# Revit family: Screen-Beam_Mounted-Teknion-JNSAFB_Fabric_Add-On-R2018
name_source: partatom
category: Furniture
revit_build: Autodesk Revit 2018 (Build: 20190510_1515(x64)
units: mm (PartAtom-declared; Revit-internal decimal feet)

## family parameters
Always vertical = Yes
Cut with Voids When Loaded = No
OmniClass Number = 23.40.20.00
OmniClass Title = General Furniture and Specialties
Room Calculation Point = No
Shared = Yes
Work Plane-Based = No

## types (2) — shared parameters
Assembly Code = E2020200
Manufacturer = Teknion
Manufacturer Fax = 416.661.4586
Part Number = JNSAFB
Product Documentation Link = http://www.teknion.com
Product Line = Expansion Cityline
Product Page URL = http://www.teknion.com
Series = Expansion Cityline
Sustainability Data = http://www.teknion.com
URL = www.teknion.com
Unit Weight URL = http://www.teknion.com
Warranty = http://www.teknion.com

## per-type parameters (varying)
| type | Base Height | Description | Low Base Height | Model | Standard Base Height |
| Standard Base Height (28") | 27.811 " | Fabric Add-On Screen – Beam-Mounted on Center, Standard Base Height (28 inches) | No | JNSAFBC_____ | Yes |
| Low Base Height (18") | 17.626 " | Fabric Add-On Screen – Beam-Mounted on Center, Low Base Height (18 inches) | Yes | JNSAFBL_____ | No |

## geometry (parser evidence)
native form markers: Sweep x2
no freeform markers — native parametric forms only
